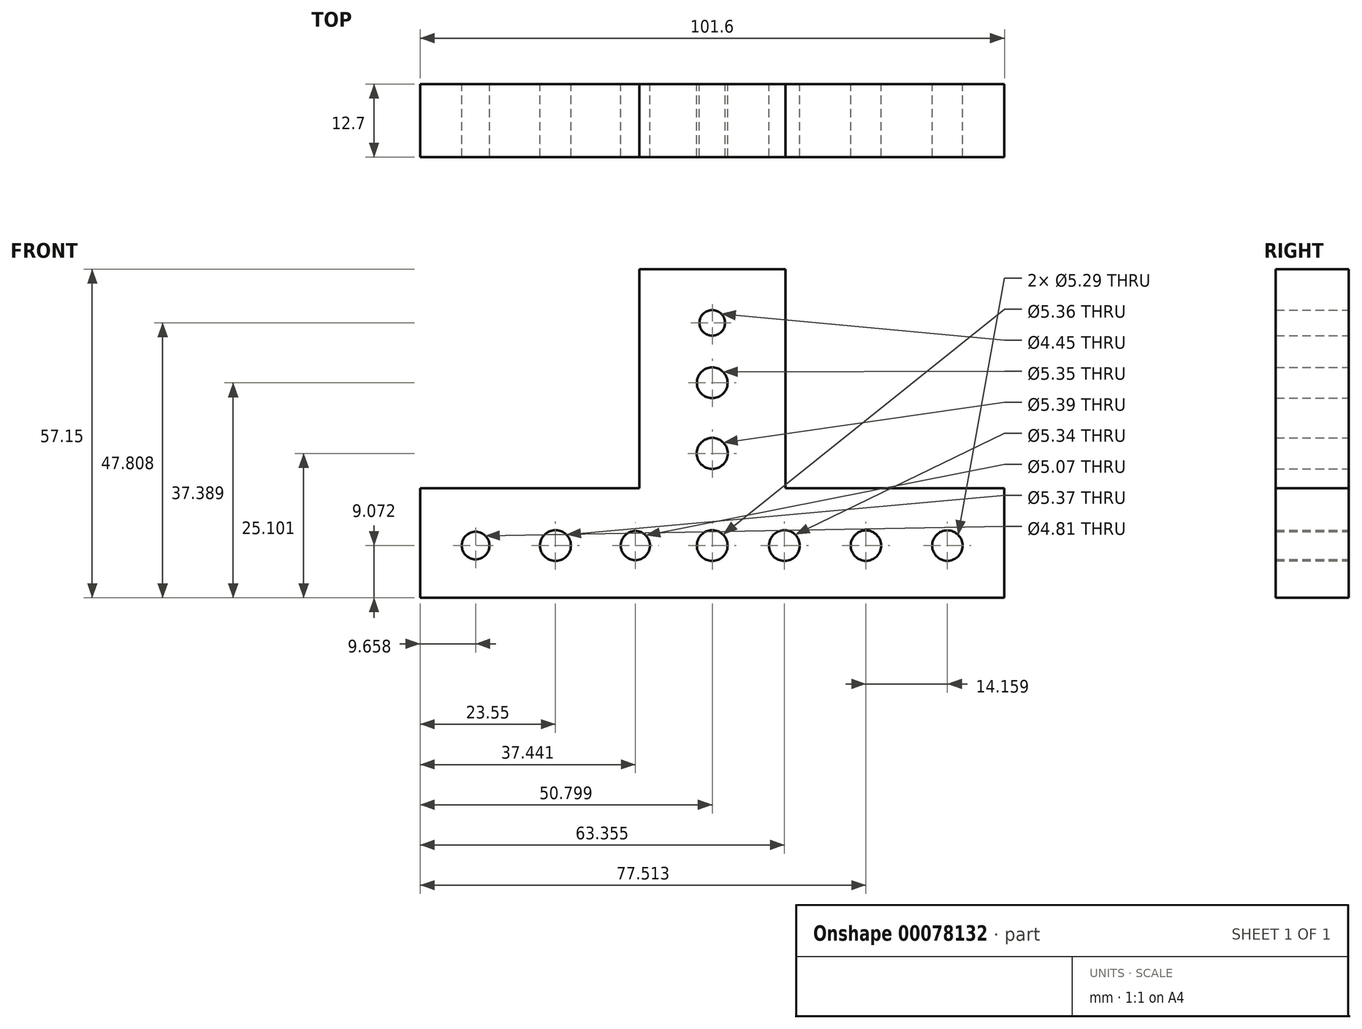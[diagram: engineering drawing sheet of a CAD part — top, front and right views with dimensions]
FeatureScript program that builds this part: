
annotation { "Feature Type Name" : "Feature", "Feature Type Description" : "" }
export const myFeature = defineFeature(function(context is Context, id is Id, definition is map)
    precondition{}
    {
        {
            var Q0;
            Q0=qCreatedBy(makeId("Front.planeOp"),FACE);
            var sketch = newSketch(context, id + "F0", { "sketchPlane" : qUnion([Q0])});
            skLineSegment(sketch, "E0", {"start": v(59.35, -15.35) * mm, "end": v(59.35, 3.7) * mm});
            skLineSegment(sketch, "E1", {"start": v(59.35, 3.7) * mm, "end": v(21.25, 3.7) * mm});
            skLineSegment(sketch, "E2", {"start": v(21.25, 3.7) * mm, "end": v(21.25, 41.8) * mm});
            skLineSegment(sketch, "E3", {"start": v(21.25, 41.8) * mm, "end": v(-4.15, 41.8) * mm});
            skLineSegment(sketch, "E4", {"start": v(-4.15, 41.8) * mm, "end": v(-4.15, 3.7) * mm});
            skLineSegment(sketch, "E5", {"start": v(-4.15, 3.7) * mm, "end": v(-42.25, 3.7) * mm});
            skLineSegment(sketch, "E6", {"start": v(-42.25, 3.7) * mm, "end": v(-42.25, -15.35) * mm});
            skLineSegment(sketch, "E7", {"start": v(-42.25, -15.35) * mm, "end": v(59.35, -15.35) * mm});
            skCircle(sketch, "E8", {"center": v(8.55, -6.28) * mm, "radius": 2.68 * mm});
            skPoint(sketch, "E8.centerSnap0", {"position": v(8.55, 41.8) * mm});
            skCircle(sketch, "E9", {"center": v(8.55, 32.46) * mm, "radius": 2.23 * mm});
            skCircle(sketch, "E10", {"center": v(8.55, 22.04) * mm, "radius": 2.67 * mm});
            skCircle(sketch, "E11", {"center": v(8.55, 9.75) * mm, "radius": 2.7 * mm});
            skCircle(sketch, "E12", {"center": v(21.1, -6.28) * mm, "radius": 2.67 * mm});
            skCircle(sketch, "E13", {"center": v(35.26, -6.28) * mm, "radius": 2.64 * mm});
            skCircle(sketch, "E14", {"center": v(49.42, -6.28) * mm, "radius": 2.64 * mm});
            skCircle(sketch, "E15", {"center": v(-4.8, -6.28) * mm, "radius": 2.53 * mm});
            skCircle(sketch, "E16", {"center": v(-18.7, -6.28) * mm, "radius": 2.68 * mm});
            skCircle(sketch, "E17", {"center": v(-32.6, -6.28) * mm, "radius": 2.4 * mm});
            skSolve(sketch);
        }
        {
            var Q0;
            Q0=makeQuery(id+"F0.imprint","IMPRINT",FACE,{"disambiguationData":[TD([[makeQuery(id+"F0.imprint","IMPRINT",EDGE,{"derivedFrom":sQuery(id+"F0.wireOp",EDGE,"E0")}),1.0]])]});
            extrude(context, id + "F1", {"entities" : qUnion([Q0]), "depth" : 12.7 * mm});
        }
    });
